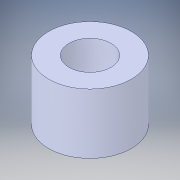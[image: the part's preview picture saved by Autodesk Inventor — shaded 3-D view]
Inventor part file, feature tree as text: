
AUTODESK INVENTOR PART (.ipt)
format: ipt  version: 2018 (Build 220112000, 112)  size: 105,472 bytes
history: native  units: in
note: dims shown in document units (in); Inventor stores cm internally (conversion verified against a paired STEP export)
features: extrude x1, sketch x1, other x1
ambient origin geometry x8: Origin, YZ Plane, XZ Plane, XY Plane, X Axis, Y Axis, Z Axis, Center Point
bodies: Solid1 (feature_tree)
feature tree (3):
  extrude  "Extrusion1"  [1 undecoded]
  sketch  "Sketch1"  dims[d0=0.305in d1=0.0in]
  other  "Boss-Extrude1"
note: 1 required parameter value undecoded (feature->parameter linkage not recoverable at this tier; creation-order binding heuristic only, values carry confidence <= 0.55)
